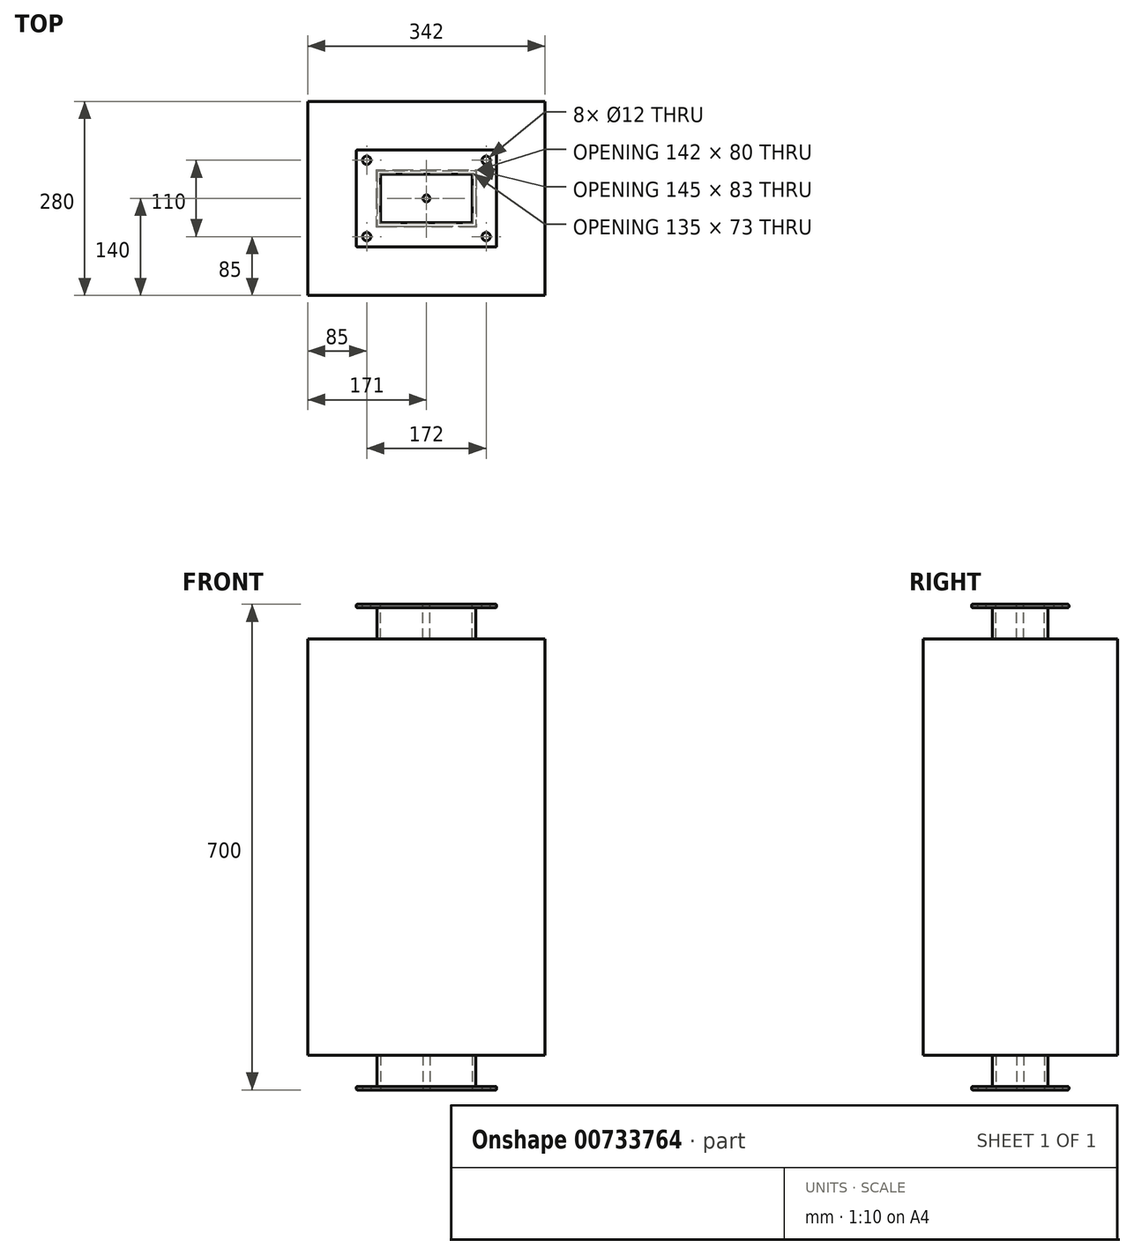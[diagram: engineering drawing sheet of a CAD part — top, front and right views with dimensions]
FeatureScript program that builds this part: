
annotation { "Feature Type Name" : "Feature", "Feature Type Description" : "" }
export const myFeature = defineFeature(function(context is Context, id is Id, definition is map)
    precondition{}
    {
        {
            var Q0;
            Q0=qCreatedBy(makeId("Top.planeOp"),FACE);
            var sketch = newSketch(context, id + "F0", { "sketchPlane" : qUnion([Q0])});
            skLineSegment(sketch, "E0.bottom", {"start": v(71, -40) * mm, "end": v(-71, -40) * mm});
            skLineSegment(sketch, "E0.top", {"start": v(71, 40) * mm, "end": v(-71, 40) * mm});
            skLineSegment(sketch, "E0.left", {"start": v(71, -40) * mm, "end": v(71, 40) * mm});
            skLineSegment(sketch, "E0.right", {"start": v(-71, -40) * mm, "end": v(-71, 40) * mm});
            skPoint(sketch, "E0.middle", {"position": v(0, 0) * mm});
            skSolve(sketch);
        }
        {
            var Q0;
            Q0=makeQuery(id+"F0.imprint","IMPRINT",FACE,{"disambiguationData":[TD([[makeQuery(id+"F0.imprint","IMPRINT",EDGE,{"derivedFrom":sQuery(id+"F0.wireOp",EDGE,"E0.bottom")}),-1.0]])]});
            extrude(context, id + "F1", {"entities" : qUnion([Q0]), "depth" : 350 * mm, "offsetDistance" : 25 * mm});
        }
        {
            var Q0;
            Q0=qCreatedBy(makeId("Top.planeOp"),FACE);
            var sketch = newSketch(context, id + "F2", { "sketchPlane" : qUnion([Q0])});
            skLineSegment(sketch, "E1.bottom", {"start": v(101, -70) * mm, "end": v(-101, -70) * mm});
            skLineSegment(sketch, "E1.top", {"start": v(101, 70) * mm, "end": v(-101, 70) * mm});
            skLineSegment(sketch, "E1.left", {"start": v(101, -70) * mm, "end": v(101, 70) * mm});
            skLineSegment(sketch, "E1.right", {"start": v(-101, -70) * mm, "end": v(-101, 70) * mm});
            skPoint(sketch, "E1.middle", {"position": v(0, 0) * mm});
            skLineSegment(sketch, "E2.0", {"start": v(66, 35) * mm, "end": v(66, -35) * mm});
            skLineSegment(sketch, "E2.1", {"start": v(-66, 35) * mm, "end": v(66, 35) * mm});
            skLineSegment(sketch, "E2.2", {"start": v(-66, -35) * mm, "end": v(-66, 35) * mm});
            skLineSegment(sketch, "E2.3", {"start": v(66, -35) * mm, "end": v(-66, -35) * mm});
            skCircle(sketch, "E3", {"center": v(0, 0) * mm, "radius": 5 * mm});
            skCircle(sketch, "E4", {"center": v(86, -55) * mm, "radius": 6 * mm});
            skCircle(sketch, "E5", {"center": v(-86, -55) * mm, "radius": 6 * mm});
            skCircle(sketch, "E6", {"center": v(-86, 55) * mm, "radius": 6 * mm});
            skCircle(sketch, "E7", {"center": v(86, 55) * mm, "radius": 6 * mm});
            skSolve(sketch);
        }
        {
            var Q0;
            Q0=makeQuery(id+"F2.imprint","IMPRINT",FACE,{"disambiguationData":[TD([[makeQuery(id+"F2.imprint","IMPRINT",EDGE,{"derivedFrom":sQuery(id+"F2.wireOp",EDGE,"E1.bottom")}),-1.0]])]});
            extrude(context, id + "F3", {"entities" : qUnion([Q0]), "depth" : 5 * mm, "offsetDistance" : 25 * mm});
        }
        {
            var Q0;
            Q0=makeQuery(id+"F1.opExtrude","SWEPT_BODY",BODY,{"disambiguationData":[OSD([sQuery(id+"F0.wireOp",EDGE,"E0.bottom"),sQuery(id+"F0.wireOp",EDGE,"E0.top"),sQuery(id+"F0.wireOp",EDGE,"E0.left"),sQuery(id+"F0.wireOp",EDGE,"E0.right")])]});
            var Q1;
            Q1=makeQuery(id+"F3.opExtrude","SWEPT_BODY",BODY,{"disambiguationData":[OSD([sQuery(id+"F2.wireOp",EDGE,"E1.bottom"),sQuery(id+"F2.wireOp",EDGE,"E1.top"),sQuery(id+"F2.wireOp",EDGE,"E1.left"),sQuery(id+"F2.wireOp",EDGE,"E1.right")])]});
            booleanBodies(context, id + "F4", {"operationType" : BooleanOperationType.UNION, "tools" : qUnion([Q0, Q1])});
        }
        {
            var Q0;
            Q0=makeQuery(id+"F2.imprint","IMPRINT",FACE,{"disambiguationData":[TD([[makeQuery(id+"F2.imprint","IMPRINT",EDGE,{"derivedFrom":sQuery(id+"F2.wireOp",EDGE,"E2.0")}),-1.0]])]});
            extrude(context, id + "F5", {"entities" : qUnion([Q0]), "operationType" : NewBodyOperationType.REMOVE, "depth" : 700 * mm, "offsetDistance" : 25 * mm});
        }
        {
            var Q0;
            Q0=makeQuery(id+"F4.opBoolean","INTERSECT",EDGE,{"derivedFrom":[makeQuery(id+"F1.opExtrude","SWEPT_FACE",FACE,{"disambiguationData":[OSD([sQuery(id+"F0.wireOp",EDGE,"E0.top")])]}),makeQuery(id+"F3.opExtrude","CAP_FACE",FACE,{"disambiguationData":[OSD([sQuery(id+"F2.wireOp",EDGE,"E1.bottom"),sQuery(id+"F2.wireOp",EDGE,"E1.top"),sQuery(id+"F2.wireOp",EDGE,"E1.left"),sQuery(id+"F2.wireOp",EDGE,"E1.right"),sQuery(id+"F2.wireOp",EDGE,"E2.0"),sQuery(id+"F2.wireOp",EDGE,"E2.1"),sQuery(id+"F2.wireOp",EDGE,"E2.2"),sQuery(id+"F2.wireOp",EDGE,"E2.3")])],"isStart":false})]});
            var Q1;
            Q1=makeQuery(id+"F3.opExtrude","CAP_EDGE",EDGE,{"disambiguationData":[OSD([sQuery(id+"F2.wireOp",EDGE,"E1.left")])],"isStart":false});
            var Q2;
            Q2=makeQuery(id+"FhIJoKqO3aSEmjx_1.opPattern","COPY",EDGE,{"derivedFrom":makeQuery(id+"F3.opExtrude","CAP_EDGE",EDGE,{"disambiguationData":[OSD([sQuery(id+"F2.wireOp",EDGE,"E1.top")])],"isStart":true}),"instanceName":"1"});
            var Q3;
            Q3=makeQuery(id+"FhIJoKqO3aSEmjx_1.opPattern","COPY",EDGE,{"derivedFrom":makeQuery(id+"F4.opBoolean","INTERSECT",EDGE,{"derivedFrom":[makeQuery(id+"F1.opExtrude","SWEPT_FACE",FACE,{"disambiguationData":[OSD([sQuery(id+"F0.wireOp",EDGE,"E0.top")])]}),makeQuery(id+"F3.opExtrude","CAP_FACE",FACE,{"disambiguationData":[OSD([sQuery(id+"F2.wireOp",EDGE,"E1.bottom"),sQuery(id+"F2.wireOp",EDGE,"E1.top"),sQuery(id+"F2.wireOp",EDGE,"E1.left"),sQuery(id+"F2.wireOp",EDGE,"E1.right"),sQuery(id+"F2.wireOp",EDGE,"E2.0"),sQuery(id+"F2.wireOp",EDGE,"E2.1"),sQuery(id+"F2.wireOp",EDGE,"E2.2"),sQuery(id+"F2.wireOp",EDGE,"E2.3")])],"isStart":false})]}),"instanceName":"1"});
            var Q4;
            Q4=makeQuery(id+"F5.boolean.opBoolean","COPY",EDGE,{"derivedFrom":makeQuery(id+"F5.opExtrude","SWEPT_EDGE",EDGE,{"disambiguationData":[OSD([sQuery(id+"F2.wireOp",EDGE,"E2.0"),sQuery(id+"F2.wireOp",EDGE,"E2.3")])]})});
            var Q5;
            Q5=makeQuery(id+"F3.opExtrude","CAP_EDGE",EDGE,{"disambiguationData":[OSD([sQuery(id+"F2.wireOp",EDGE,"E1.top")])],"isStart":true});
            var Q6;
            Q6=makeQuery(id+"FhIJoKqO3aSEmjx_1.opPattern","COPY",EDGE,{"derivedFrom":makeQuery(id+"F3.opExtrude","CAP_EDGE",EDGE,{"disambiguationData":[OSD([sQuery(id+"F2.wireOp",EDGE,"E1.right")])],"isStart":true}),"instanceName":"1"});
            var Q7;
            Q7=makeQuery(id+"FhIJoKqO3aSEmjx_1.opPattern","COPY",EDGE,{"derivedFrom":makeQuery(id+"F3.opExtrude","CAP_EDGE",EDGE,{"disambiguationData":[OSD([sQuery(id+"F2.wireOp",EDGE,"E1.bottom")])],"isStart":false}),"instanceName":"1"});
            var Q8;
            Q8=makeQuery(id+"FhIJoKqO3aSEmjx_1.opPattern","COPY",EDGE,{"derivedFrom":makeQuery(id+"F3.opExtrude","SWEPT_EDGE",EDGE,{"disambiguationData":[OSD([sQuery(id+"F2.wireOp",EDGE,"E1.top"),sQuery(id+"F2.wireOp",EDGE,"E1.left")])]}),"instanceName":"1"});
            var Q9;
            Q9=makeQuery(id+"FhIJoKqO3aSEmjx_1.opPattern","COPY",EDGE,{"derivedFrom":makeQuery(id+"F3.opExtrude","CAP_EDGE",EDGE,{"disambiguationData":[OSD([sQuery(id+"F2.wireOp",EDGE,"E1.top")])],"isStart":false}),"instanceName":"1"});
            var Q10;
            {var subQ0=makeQuery(id+"F1.opExtrude","SWEPT_EDGE",EDGE,{"disambiguationData":[OSD([sQuery(id+"F0.wireOp",EDGE,"E0.bottom"),sQuery(id+"F0.wireOp",EDGE,"E0.left")])]});Q10=makeQuery(id+"FhIJoKqO3aSEmjx_1.boolean.opBoolean","MERGE",EDGE,{"derivedFrom":[subQ0,makeQuery(id+"FhIJoKqO3aSEmjx_1.opPattern","COPY",EDGE,{"derivedFrom":subQ0,"instanceName":"1"})]});}
            var Q11;
            Q11=makeQuery(id+"F5.boolean.opBoolean","COPY",EDGE,{"derivedFrom":makeQuery(id+"F5.opExtrude","SWEPT_EDGE",EDGE,{"disambiguationData":[OSD([sQuery(id+"F2.wireOp",EDGE,"E2.0"),sQuery(id+"F2.wireOp",EDGE,"E2.1")])]})});
            var Q12;
            Q12=makeQuery(id+"F4.opBoolean","INTERSECT",EDGE,{"derivedFrom":[makeQuery(id+"F1.opExtrude","SWEPT_FACE",FACE,{"disambiguationData":[OSD([sQuery(id+"F0.wireOp",EDGE,"E0.left")])]}),makeQuery(id+"F3.opExtrude","CAP_FACE",FACE,{"disambiguationData":[OSD([sQuery(id+"F2.wireOp",EDGE,"E1.bottom"),sQuery(id+"F2.wireOp",EDGE,"E1.top"),sQuery(id+"F2.wireOp",EDGE,"E1.left"),sQuery(id+"F2.wireOp",EDGE,"E1.right"),sQuery(id+"F2.wireOp",EDGE,"E2.0"),sQuery(id+"F2.wireOp",EDGE,"E2.1"),sQuery(id+"F2.wireOp",EDGE,"E2.2"),sQuery(id+"F2.wireOp",EDGE,"E2.3")])],"isStart":false})]});
            var Q13;
            Q13=makeQuery(id+"F3.opExtrude","SWEPT_EDGE",EDGE,{"disambiguationData":[OSD([sQuery(id+"F2.wireOp",EDGE,"E1.bottom"),sQuery(id+"F2.wireOp",EDGE,"E1.left")])]});
            var Q14;
            Q14=makeQuery(id+"FhIJoKqO3aSEmjx_1.opPattern","COPY",EDGE,{"derivedFrom":makeQuery(id+"F3.opExtrude","CAP_EDGE",EDGE,{"disambiguationData":[OSD([sQuery(id+"F2.wireOp",EDGE,"E1.bottom")])],"isStart":true}),"instanceName":"1"});
            var Q15;
            Q15=makeQuery(id+"FhIJoKqO3aSEmjx_1.opPattern","COPY",EDGE,{"derivedFrom":makeQuery(id+"F3.opExtrude","CAP_EDGE",EDGE,{"disambiguationData":[OSD([sQuery(id+"F2.wireOp",EDGE,"E1.right")])],"isStart":false}),"instanceName":"1"});
            var Q16;
            {var subQ0=makeQuery(id+"F1.opExtrude","SWEPT_EDGE",EDGE,{"disambiguationData":[OSD([sQuery(id+"F0.wireOp",EDGE,"E0.top"),sQuery(id+"F0.wireOp",EDGE,"E0.right")])]});Q16=makeQuery(id+"FhIJoKqO3aSEmjx_1.boolean.opBoolean","MERGE",EDGE,{"derivedFrom":[subQ0,makeQuery(id+"FhIJoKqO3aSEmjx_1.opPattern","COPY",EDGE,{"derivedFrom":subQ0,"instanceName":"1"})]});}
            var Q17;
            Q17=makeQuery(id+"F3.opExtrude","CAP_EDGE",EDGE,{"disambiguationData":[OSD([sQuery(id+"F2.wireOp",EDGE,"E1.right")])],"isStart":false});
            var Q18;
            Q18=makeQuery(id+"FhIJoKqO3aSEmjx_1.opPattern","COPY",EDGE,{"derivedFrom":makeQuery(id+"F3.opExtrude","CAP_EDGE",EDGE,{"disambiguationData":[OSD([sQuery(id+"F2.wireOp",EDGE,"E1.left")])],"isStart":true}),"instanceName":"1"});
            var Q19;
            Q19=makeQuery(id+"FhIJoKqO3aSEmjx_1.opPattern","COPY",EDGE,{"derivedFrom":makeQuery(id+"F3.opExtrude","CAP_EDGE",EDGE,{"disambiguationData":[OSD([sQuery(id+"F2.wireOp",EDGE,"E1.left")])],"isStart":false}),"instanceName":"1"});
            var Q20;
            Q20=makeQuery(id+"F3.opExtrude","CAP_EDGE",EDGE,{"disambiguationData":[OSD([sQuery(id+"F2.wireOp",EDGE,"E1.bottom")])],"isStart":true});
            var Q21;
            Q21=makeQuery(id+"FhIJoKqO3aSEmjx_1.opPattern","COPY",EDGE,{"derivedFrom":makeQuery(id+"F4.opBoolean","INTERSECT",EDGE,{"derivedFrom":[makeQuery(id+"F1.opExtrude","SWEPT_FACE",FACE,{"disambiguationData":[OSD([sQuery(id+"F0.wireOp",EDGE,"E0.left")])]}),makeQuery(id+"F3.opExtrude","CAP_FACE",FACE,{"disambiguationData":[OSD([sQuery(id+"F2.wireOp",EDGE,"E1.bottom"),sQuery(id+"F2.wireOp",EDGE,"E1.top"),sQuery(id+"F2.wireOp",EDGE,"E1.left"),sQuery(id+"F2.wireOp",EDGE,"E1.right"),sQuery(id+"F2.wireOp",EDGE,"E2.0"),sQuery(id+"F2.wireOp",EDGE,"E2.1"),sQuery(id+"F2.wireOp",EDGE,"E2.2"),sQuery(id+"F2.wireOp",EDGE,"E2.3")])],"isStart":false})]}),"instanceName":"1"});
            var Q22;
            Q22=makeQuery(id+"F3.opExtrude","CAP_EDGE",EDGE,{"disambiguationData":[OSD([sQuery(id+"F2.wireOp",EDGE,"E1.left")])],"isStart":true});
            var Q23;
            {var subQ0=makeQuery(id+"F1.opExtrude","SWEPT_EDGE",EDGE,{"disambiguationData":[OSD([sQuery(id+"F0.wireOp",EDGE,"E0.top"),sQuery(id+"F0.wireOp",EDGE,"E0.left")])]});Q23=makeQuery(id+"FhIJoKqO3aSEmjx_1.boolean.opBoolean","MERGE",EDGE,{"derivedFrom":[subQ0,makeQuery(id+"FhIJoKqO3aSEmjx_1.opPattern","COPY",EDGE,{"derivedFrom":subQ0,"instanceName":"1"})]});}
            var Q24;
            Q24=makeQuery(id+"FhIJoKqO3aSEmjx_1.opPattern","COPY",EDGE,{"derivedFrom":makeQuery(id+"F3.opExtrude","SWEPT_EDGE",EDGE,{"disambiguationData":[OSD([sQuery(id+"F2.wireOp",EDGE,"E1.bottom"),sQuery(id+"F2.wireOp",EDGE,"E1.left")])]}),"instanceName":"1"});
            var Q25;
            Q25=makeQuery(id+"F3.opExtrude","CAP_EDGE",EDGE,{"disambiguationData":[OSD([sQuery(id+"F2.wireOp",EDGE,"E1.top")])],"isStart":false});
            var Q26;
            Q26=makeQuery(id+"F3.opExtrude","SWEPT_EDGE",EDGE,{"disambiguationData":[OSD([sQuery(id+"F2.wireOp",EDGE,"E1.top"),sQuery(id+"F2.wireOp",EDGE,"E1.left")])]});
            var Q27;
            Q27=makeQuery(id+"F3.opExtrude","CAP_EDGE",EDGE,{"disambiguationData":[OSD([sQuery(id+"F2.wireOp",EDGE,"E1.right")])],"isStart":true});
            var Q28;
            Q28=makeQuery(id+"F3.opExtrude","CAP_EDGE",EDGE,{"disambiguationData":[OSD([sQuery(id+"F2.wireOp",EDGE,"E1.bottom")])],"isStart":false});
            var Q29;
            Q29=makeQuery(id+"F5.boolean.opBoolean","COPY",EDGE,{"derivedFrom":makeQuery(id+"F5.opExtrude","SWEPT_EDGE",EDGE,{"disambiguationData":[OSD([sQuery(id+"F2.wireOp",EDGE,"E2.1"),sQuery(id+"F2.wireOp",EDGE,"E2.2")])]})});
            var Q30;
            Q30=makeQuery(id+"F5.boolean.opBoolean","COPY",EDGE,{"derivedFrom":makeQuery(id+"F5.opExtrude","SWEPT_EDGE",EDGE,{"disambiguationData":[OSD([sQuery(id+"F2.wireOp",EDGE,"E2.2"),sQuery(id+"F2.wireOp",EDGE,"E2.3")])]})});
            var Q31;
            Q31=makeQuery(id+"F5.boolean.opBoolean","COPY",EDGE,{"derivedFrom":makeQuery(id+"F5.opExtrude","CAP_EDGE",EDGE,{"disambiguationData":[OSD([sQuery(id+"F2.wireOp",EDGE,"E2.0")])],"isStart":false})});
            var Q32;
            Q32=makeQuery(id+"F5.boolean.opBoolean","COPY",EDGE,{"derivedFrom":makeQuery(id+"F5.opExtrude","CAP_EDGE",EDGE,{"disambiguationData":[OSD([sQuery(id+"F2.wireOp",EDGE,"E2.1")])],"isStart":true})});
            var Q33;
            Q33=makeQuery(id+"F5.boolean.opBoolean","COPY",EDGE,{"derivedFrom":makeQuery(id+"F5.opExtrude","CAP_EDGE",EDGE,{"disambiguationData":[OSD([sQuery(id+"F2.wireOp",EDGE,"E2.1")])],"isStart":false})});
            var Q34;
            Q34=makeQuery(id+"F5.boolean.opBoolean","COPY",EDGE,{"derivedFrom":makeQuery(id+"F5.opExtrude","CAP_EDGE",EDGE,{"disambiguationData":[OSD([sQuery(id+"F2.wireOp",EDGE,"E2.2")])],"isStart":false})});
            var Q35;
            Q35=makeQuery(id+"F5.boolean.opBoolean","COPY",EDGE,{"derivedFrom":makeQuery(id+"F5.opExtrude","CAP_EDGE",EDGE,{"disambiguationData":[OSD([sQuery(id+"F2.wireOp",EDGE,"E2.3")])],"isStart":true})});
            var Q36;
            Q36=makeQuery(id+"F5.boolean.opBoolean","COPY",EDGE,{"derivedFrom":makeQuery(id+"F5.opExtrude","CAP_EDGE",EDGE,{"disambiguationData":[OSD([sQuery(id+"F2.wireOp",EDGE,"E2.3")])],"isStart":false})});
            var Q37;
            Q37=makeQuery(id+"F4.opBoolean","INTERSECT",EDGE,{"derivedFrom":[makeQuery(id+"F1.opExtrude","SWEPT_FACE",FACE,{"disambiguationData":[OSD([sQuery(id+"F0.wireOp",EDGE,"E0.bottom")])]}),makeQuery(id+"F3.opExtrude","CAP_FACE",FACE,{"disambiguationData":[OSD([sQuery(id+"F2.wireOp",EDGE,"E1.bottom"),sQuery(id+"F2.wireOp",EDGE,"E1.top"),sQuery(id+"F2.wireOp",EDGE,"E1.left"),sQuery(id+"F2.wireOp",EDGE,"E1.right"),sQuery(id+"F2.wireOp",EDGE,"E2.0"),sQuery(id+"F2.wireOp",EDGE,"E2.1"),sQuery(id+"F2.wireOp",EDGE,"E2.2"),sQuery(id+"F2.wireOp",EDGE,"E2.3")])],"isStart":false})]});
            var Q38;
            Q38=makeQuery(id+"FhIJoKqO3aSEmjx_1.opPattern","COPY",EDGE,{"derivedFrom":makeQuery(id+"F3.opExtrude","SWEPT_EDGE",EDGE,{"disambiguationData":[OSD([sQuery(id+"F2.wireOp",EDGE,"E1.top"),sQuery(id+"F2.wireOp",EDGE,"E1.right")])]}),"instanceName":"1"});
            var Q39;
            Q39=makeQuery(id+"FhIJoKqO3aSEmjx_1.opPattern","COPY",EDGE,{"derivedFrom":makeQuery(id+"F3.opExtrude","SWEPT_EDGE",EDGE,{"disambiguationData":[OSD([sQuery(id+"F2.wireOp",EDGE,"E1.bottom"),sQuery(id+"F2.wireOp",EDGE,"E1.right")])]}),"instanceName":"1"});
            var Q40;
            Q40=makeQuery(id+"F4.opBoolean","INTERSECT",EDGE,{"derivedFrom":[makeQuery(id+"F1.opExtrude","SWEPT_FACE",FACE,{"disambiguationData":[OSD([sQuery(id+"F0.wireOp",EDGE,"E0.right")])]}),makeQuery(id+"F3.opExtrude","CAP_FACE",FACE,{"disambiguationData":[OSD([sQuery(id+"F2.wireOp",EDGE,"E1.bottom"),sQuery(id+"F2.wireOp",EDGE,"E1.top"),sQuery(id+"F2.wireOp",EDGE,"E1.left"),sQuery(id+"F2.wireOp",EDGE,"E1.right"),sQuery(id+"F2.wireOp",EDGE,"E2.0"),sQuery(id+"F2.wireOp",EDGE,"E2.1"),sQuery(id+"F2.wireOp",EDGE,"E2.2"),sQuery(id+"F2.wireOp",EDGE,"E2.3")])],"isStart":false})]});
            var Q41;
            Q41=makeQuery(id+"FhIJoKqO3aSEmjx_1.opPattern","COPY",EDGE,{"derivedFrom":makeQuery(id+"F4.opBoolean","INTERSECT",EDGE,{"derivedFrom":[makeQuery(id+"F1.opExtrude","SWEPT_FACE",FACE,{"disambiguationData":[OSD([sQuery(id+"F0.wireOp",EDGE,"E0.right")])]}),makeQuery(id+"F3.opExtrude","CAP_FACE",FACE,{"disambiguationData":[OSD([sQuery(id+"F2.wireOp",EDGE,"E1.bottom"),sQuery(id+"F2.wireOp",EDGE,"E1.top"),sQuery(id+"F2.wireOp",EDGE,"E1.left"),sQuery(id+"F2.wireOp",EDGE,"E1.right"),sQuery(id+"F2.wireOp",EDGE,"E2.0"),sQuery(id+"F2.wireOp",EDGE,"E2.1"),sQuery(id+"F2.wireOp",EDGE,"E2.2"),sQuery(id+"F2.wireOp",EDGE,"E2.3")])],"isStart":false})]}),"instanceName":"1"});
            var Q42;
            {var subQ0=makeQuery(id+"F1.opExtrude","SWEPT_EDGE",EDGE,{"disambiguationData":[OSD([sQuery(id+"F0.wireOp",EDGE,"E0.bottom"),sQuery(id+"F0.wireOp",EDGE,"E0.right")])]});Q42=makeQuery(id+"FhIJoKqO3aSEmjx_1.boolean.opBoolean","MERGE",EDGE,{"derivedFrom":[subQ0,makeQuery(id+"FhIJoKqO3aSEmjx_1.opPattern","COPY",EDGE,{"derivedFrom":subQ0,"instanceName":"1"})]});}
            var Q43;
            Q43=makeQuery(id+"FhIJoKqO3aSEmjx_1.opPattern","COPY",EDGE,{"derivedFrom":makeQuery(id+"F4.opBoolean","INTERSECT",EDGE,{"derivedFrom":[makeQuery(id+"F1.opExtrude","SWEPT_FACE",FACE,{"disambiguationData":[OSD([sQuery(id+"F0.wireOp",EDGE,"E0.bottom")])]}),makeQuery(id+"F3.opExtrude","CAP_FACE",FACE,{"disambiguationData":[OSD([sQuery(id+"F2.wireOp",EDGE,"E1.bottom"),sQuery(id+"F2.wireOp",EDGE,"E1.top"),sQuery(id+"F2.wireOp",EDGE,"E1.left"),sQuery(id+"F2.wireOp",EDGE,"E1.right"),sQuery(id+"F2.wireOp",EDGE,"E2.0"),sQuery(id+"F2.wireOp",EDGE,"E2.1"),sQuery(id+"F2.wireOp",EDGE,"E2.2"),sQuery(id+"F2.wireOp",EDGE,"E2.3")])],"isStart":false})]}),"instanceName":"1"});
            var Q44;
            Q44=makeQuery(id+"F3.opExtrude","SWEPT_EDGE",EDGE,{"disambiguationData":[OSD([sQuery(id+"F2.wireOp",EDGE,"E1.bottom"),sQuery(id+"F2.wireOp",EDGE,"E1.right")])]});
            var Q45;
            Q45=makeQuery(id+"F3.opExtrude","SWEPT_EDGE",EDGE,{"disambiguationData":[OSD([sQuery(id+"F2.wireOp",EDGE,"E1.top"),sQuery(id+"F2.wireOp",EDGE,"E1.right")])]});
            var Q46;
            Q46=makeQuery(id+"F5.boolean.opBoolean","COPY",EDGE,{"derivedFrom":makeQuery(id+"F5.opExtrude","CAP_EDGE",EDGE,{"disambiguationData":[OSD([sQuery(id+"F2.wireOp",EDGE,"E2.0")])],"isStart":true})});
            var Q47;
            Q47=makeQuery(id+"F5.boolean.opBoolean","COPY",EDGE,{"derivedFrom":makeQuery(id+"F5.opExtrude","CAP_EDGE",EDGE,{"disambiguationData":[OSD([sQuery(id+"F2.wireOp",EDGE,"E2.2")])],"isStart":true})});
            fillet(context, id + "F6", {"entities" : qUnion([Q0, Q1, Q2, Q3, Q4, Q5, Q6, Q7, Q8, Q9, Q10, Q11, Q12, Q13, Q14, Q15, Q16, Q17, Q18, Q19, Q20, Q21, Q22, Q23, Q24, Q25, Q26, Q27, Q28, Q29, Q30, Q31, Q32, Q33, Q34, Q35, Q36, Q37, Q38, Q39, Q40, Q41, Q42, Q43, Q44, Q45, Q46, Q47]), "radius" : 1.5 * mm, "tangentPropagation" : true, "allowEdgeOverflow" : false});
        }
        {
            var Q0;
            Q0=makeQuery(id+"F1.opExtrude","CAP_FACE",FACE,{"disambiguationData":[OSD([sQuery(id+"F0.wireOp",EDGE,"E0.bottom"),sQuery(id+"F0.wireOp",EDGE,"E0.top"),sQuery(id+"F0.wireOp",EDGE,"E0.left"),sQuery(id+"F0.wireOp",EDGE,"E0.right")])],"isStart":false});
            var sketch = newSketch(context, id + "F7", { "sketchPlane" : qUnion([Q0])});
            skLineSegment(sketch, "E8.bottom", {"start": v(171, -140) * mm, "end": v(-171, -140) * mm});
            skLineSegment(sketch, "E8.top", {"start": v(171, 140) * mm, "end": v(-171, 140) * mm});
            skLineSegment(sketch, "E8.left", {"start": v(171, -140) * mm, "end": v(171, 140) * mm});
            skLineSegment(sketch, "E8.right", {"start": v(-171, -140) * mm, "end": v(-171, 140) * mm});
            skPoint(sketch, "E8.middle", {"position": v(0, 0) * mm});
            skSolve(sketch);
        }
        {
            var Q0;
            Q0=qSketchRegion(id+"F7",true);
            extrude(context, id + "F8", {"entities" : qUnion([Q0]), "oppositeDirection" : true, "depth" : 300 * mm, "offsetDistance" : 25 * mm});
        }
        {
            var Q0;
            Q0=makeQuery(id+"F8.opExtrude","SWEPT_BODY",BODY,{"disambiguationData":[OSD([sQuery(id+"F7.wireOp",EDGE,"E8.bottom"),sQuery(id+"F7.wireOp",EDGE,"E8.top"),sQuery(id+"F7.wireOp",EDGE,"E8.left"),sQuery(id+"F7.wireOp",EDGE,"E8.right")])]});
            var Q1;
            Q1=makeQuery(id+"F5.boolean.opBoolean","SPLIT",BODY,{"disambiguationData":[OD(1.0)],"derivedFrom":makeQuery(id+"F1.opExtrude","SWEPT_BODY",BODY,{"disambiguationData":[OSD([sQuery(id+"F0.wireOp",EDGE,"E0.bottom"),sQuery(id+"F0.wireOp",EDGE,"E0.top"),sQuery(id+"F0.wireOp",EDGE,"E0.left"),sQuery(id+"F0.wireOp",EDGE,"E0.right")])]})});
            var Q2;
            Q2=makeQuery(id+"F5.boolean.opBoolean","SPLIT",BODY,{"disambiguationData":[OD(0.0)],"derivedFrom":makeQuery(id+"F1.opExtrude","SWEPT_BODY",BODY,{"disambiguationData":[OSD([sQuery(id+"F0.wireOp",EDGE,"E0.bottom"),sQuery(id+"F0.wireOp",EDGE,"E0.top"),sQuery(id+"F0.wireOp",EDGE,"E0.left"),sQuery(id+"F0.wireOp",EDGE,"E0.right")])]})});
            var Q3;
            Q3=makeQuery(id+"F8.opExtrude","CAP_FACE",FACE,{"disambiguationData":[OSD([sQuery(id+"F7.wireOp",EDGE,"E8.bottom"),sQuery(id+"F7.wireOp",EDGE,"E8.top"),sQuery(id+"F7.wireOp",EDGE,"E8.left"),sQuery(id+"F7.wireOp",EDGE,"E8.right")])],"isStart":true});
            mirror(context, id + "F9", {"operationType" : NewBodyOperationType.ADD, "entities" : qUnion([Q0, Q1, Q2]), "mirrorPlane" : qUnion([Q3])});
        }
    });
